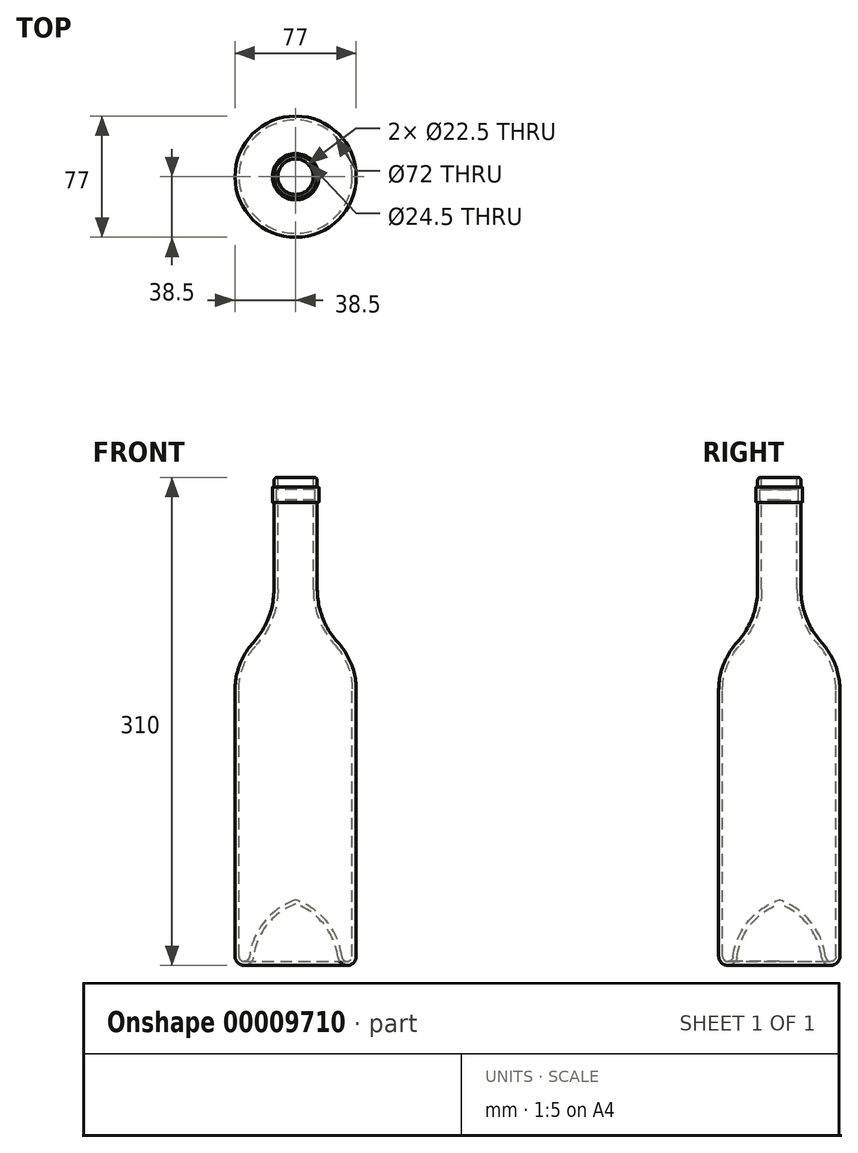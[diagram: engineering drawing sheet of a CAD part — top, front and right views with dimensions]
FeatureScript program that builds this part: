
annotation { "Feature Type Name" : "Feature", "Feature Type Description" : "" }
export const myFeature = defineFeature(function(context is Context, id is Id, definition is map)
    precondition{}
    {
        {
            var Q0;
            Q0=qCreatedBy(makeId("Front.planeOp"),FACE);
            var sketch = newSketch(context, id + "F0", { "sketchPlane" : qUnion([Q0])});
            skLineSegment(sketch, "E0", {"start": v(-38.5, -33.18) * mm, "end": v(-38.5, 136) * mm});
            skArc(sketch, "E1", {"start": v(-26.83, 166.14) * mm, "mid": v(-35.48, 152.16) * mm, "end": v(-38.5, 136) * mm});
            skArc(sketch, "E2", {"start": v(-26.83, 166.14) * mm, "mid": v(-17.14, 181.83) * mm, "end": v(-13.75, 199.95) * mm});
            skLineSegment(sketch, "E3", {"start": v(-13.75, 199.95) * mm, "end": v(-13.75, 255) * mm});
            skLineSegment(sketch, "E4", {"start": v(0, 271) * mm, "end": v(0, 0) * mm});
            skLineSegment(sketch, "E5", {"start": v(-59.73, -39) * mm, "end": v(296.58, -39) * mm, "construction": true});
            skArc(sketch, "E6", {"start": v(0, 0) * mm, "mid": v(-18.2, -13.2) * mm, "end": v(-26.9, -33.91) * mm});
            skLineSegment(sketch, "E7", {"start": v(-13.75, 255) * mm, "end": v(-14.75, 255) * mm});
            skLineSegment(sketch, "E8", {"start": v(-14.75, 255) * mm, "end": v(-14.75, 265) * mm});
            skLineSegment(sketch, "E9", {"start": v(-14.75, 265) * mm, "end": v(-13.75, 265) * mm});
            skLineSegment(sketch, "E10", {"start": v(-13.75, 265) * mm, "end": v(-13.75, 271) * mm});
            skLineSegment(sketch, "E11", {"start": v(-13.75, 271) * mm, "end": v(0, 271) * mm});
            skArc(sketch, "E12", {"start": v(-38.5, -33.18) * mm, "mid": v(-33.05, -38.99) * mm, "end": v(-26.9, -33.91) * mm});
            skSolve(sketch);
        }
        {
            var Q0;
            Q0 = qSketchRegion(id + "F0", true);
            var Q1;
            Q1=sQuery(id+"F0.wireOp",EDGE,"E4");
            revolve(context, id + "F1", {"entities" : qUnion([Q0]), "axis" : qUnion([Q1]), "revolveType" : RevolveType.FULL});
        }
        {
            var Q0;
            Q0=makeQuery(id+"F1.opRevolve","SWEPT_EDGE",EDGE,{"disambiguationData":[OSD([sQuery(id+"F0.wireOp",EDGE,"E9"),sQuery(id+"F0.wireOp",EDGE,"E10")])]});
            var Q1;
            Q1=makeQuery(id+"F1.opRevolve","SWEPT_EDGE",EDGE,{"disambiguationData":[OSD([sQuery(id+"F0.wireOp",EDGE,"E8"),sQuery(id+"F0.wireOp",EDGE,"E9")])]});
            var Q2;
            Q2=makeQuery(id+"F1.opRevolve","SWEPT_EDGE",EDGE,{"disambiguationData":[OSD([sQuery(id+"F0.wireOp",EDGE,"E7"),sQuery(id+"F0.wireOp",EDGE,"E8")])]});
            var Q3;
            Q3=makeQuery(id+"F1.opRevolve","SWEPT_EDGE",EDGE,{"disambiguationData":[OSD([sQuery(id+"F0.wireOp",EDGE,"E3"),sQuery(id+"F0.wireOp",EDGE,"E7")])]});
            fillet(context, id + "F2", {"entities" : qUnion([Q0, Q1, Q2, Q3]), "radius" : .5 * mm, "tangentPropagation" : true, "allowEdgeOverflow" : false});
        }
        {
            var Q0;
            Q0=makeQuery(id+"F1.opRevolve","SWEPT_EDGE",EDGE,{"disambiguationData":[OSD([sQuery(id+"F0.wireOp",EDGE,"E10"),sQuery(id+"F0.wireOp",EDGE,"E11")])]});
            fillet(context, id + "F3", {"entities" : qUnion([Q0]), "radius" : 2 * mm, "tangentPropagation" : true, "allowEdgeOverflow" : false});
        }
        {
            var Q0;
            Q0=makeQuery(id+"F1.opRevolve","SWEPT_FACE",FACE,{"disambiguationData":[OSD([sQuery(id+"F0.wireOp",EDGE,"E11")])]});
            shell(context, id + "F4", {"entities" : qUnion([Q0]), "thickness" : 2.5 * mm});
        }
        {
            var Q0;
            Q0=makeQuery(id+"F4.opShell","OFFSET_EDGE",EDGE,{"disambiguationData":[OSD([sQuery(id+"F0.wireOp",EDGE,"E10"),sQuery(id+"F0.wireOp",EDGE,"E11")])]});
            fillet(context, id + "F5", {"entities" : qUnion([Q0]), "radius" : .5 * mm, "tangentPropagation" : true, "allowEdgeOverflow" : false});
        }
    });
